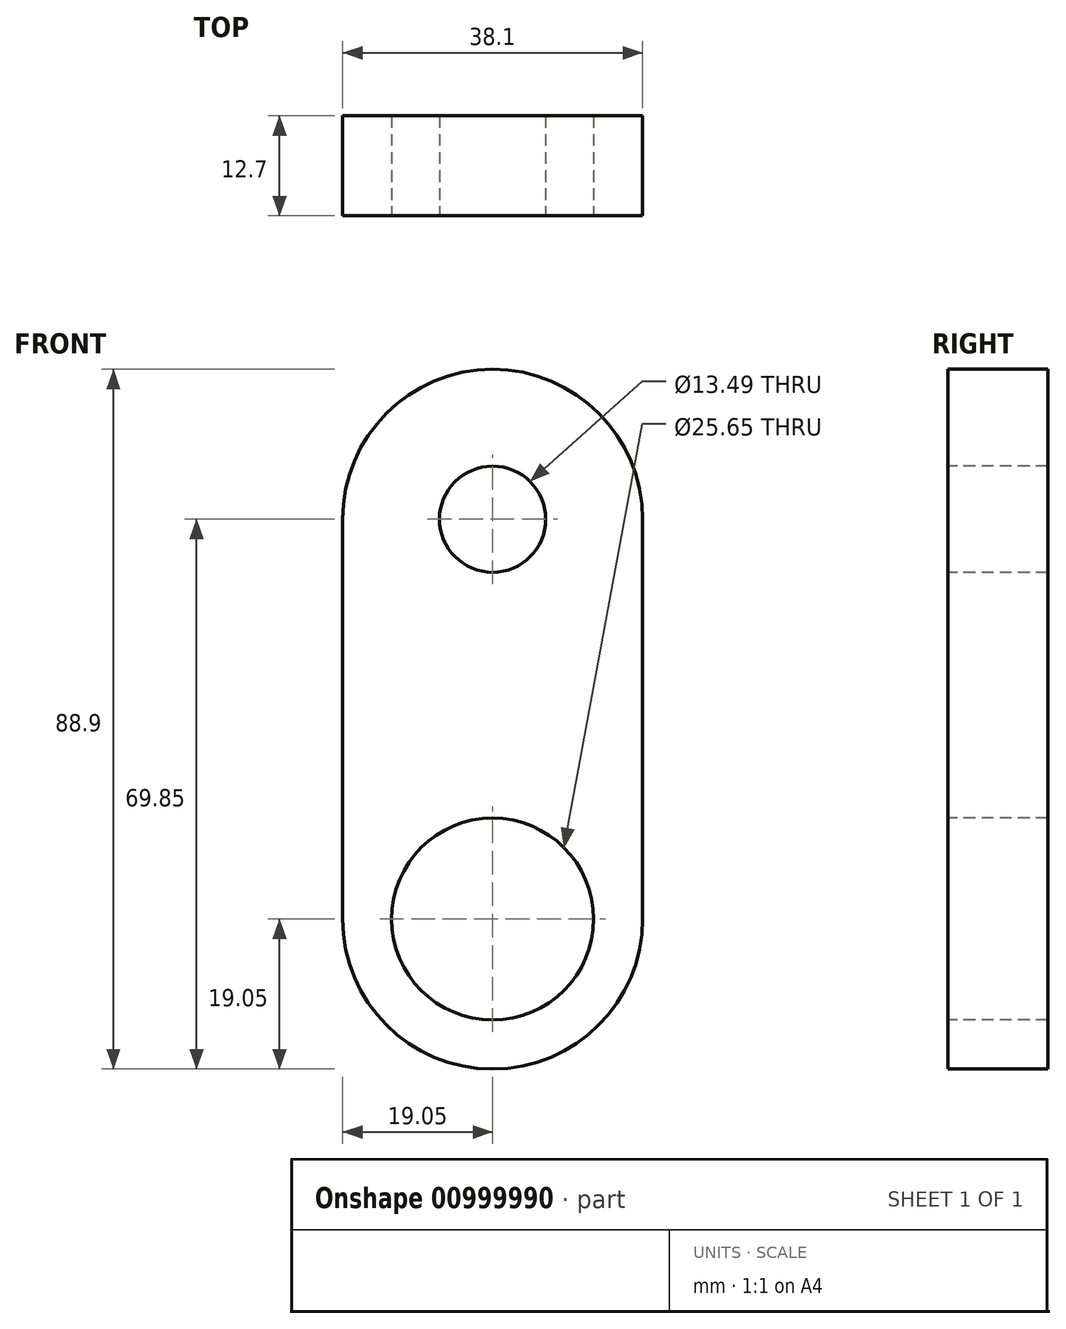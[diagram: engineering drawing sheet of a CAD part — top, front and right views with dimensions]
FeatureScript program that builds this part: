
annotation { "Feature Type Name" : "Feature", "Feature Type Description" : "" }
export const myFeature = defineFeature(function(context is Context, id is Id, definition is map)
    precondition{}
    {
        {
            var Q0;
            Q0=qCreatedBy(makeId("Front.planeOp"),FACE);
            var sketch = newSketch(context, id + "F0", { "sketchPlane" : qUnion([Q0])});
            skCircle(sketch, "E0", {"center": v(0, 0) * mm, "radius": 19.05 * mm});
            skLineSegment(sketch, "E1.bottom", {"start": v(-19.05, 0) * mm, "end": v(19.05, 0) * mm});
            skLineSegment(sketch, "E1.top", {"start": v(-19.05, 50.8) * mm, "end": v(19.05, 50.8) * mm});
            skLineSegment(sketch, "E1.left", {"start": v(-19.05, 0) * mm, "end": v(-19.05, 50.8) * mm});
            skLineSegment(sketch, "E1.right", {"start": v(19.05, 0) * mm, "end": v(19.05, 50.8) * mm});
            skCircle(sketch, "E2", {"center": v(0, 50.8) * mm, "radius": 19.05 * mm});
            skSolve(sketch);
        }
        {
            var Q0;
            {var subQ0=sQuery(id+"F0.wireOp",EDGE,"E1.top");Q0=makeQuery(id+"F0.imprint","IMPRINT",FACE,{"disambiguationData":[TD([[makeQuery(id+"F0.imprint","IMPRINT",EDGE,{"derivedFrom":subQ0}),1.0]])]});}
            var Q1;
            {var subQ0=sQuery(id+"F0.wireOp",EDGE,"E1.top");Q1=makeQuery(id+"F0.imprint","IMPRINT",FACE,{"disambiguationData":[TD([[makeQuery(id+"F0.imprint","IMPRINT",EDGE,{"derivedFrom":subQ0}),-1.0]])]});}
            var Q2;
            {var subQ0=sQuery(id+"F0.wireOp",EDGE,"E1.left");Q2=makeQuery(id+"F0.imprint","IMPRINT",FACE,{"disambiguationData":[TD([[makeQuery(id+"F0.imprint","IMPRINT",EDGE,{"derivedFrom":subQ0}),-1.0]])]});}
            var Q3;
            {var subQ0=sQuery(id+"F0.wireOp",EDGE,"E1.bottom");Q3=makeQuery(id+"F0.imprint","IMPRINT",FACE,{"disambiguationData":[TD([[makeQuery(id+"F0.imprint","IMPRINT",EDGE,{"derivedFrom":subQ0}),1.0]])]});}
            var Q4;
            {var subQ0=sQuery(id+"F0.wireOp",EDGE,"E1.bottom");Q4=makeQuery(id+"F0.imprint","IMPRINT",FACE,{"disambiguationData":[TD([[makeQuery(id+"F0.imprint","IMPRINT",EDGE,{"derivedFrom":subQ0}),-1.0]])]});}
            extrude(context, id + "F1", {"entities" : qUnion([Q0, Q1, Q2, Q3, Q4]), "depth" : 12.7 * mm, "offsetDistance" : 25.4 * mm});
        }
        {
            var Q0;
            Q0=makeQuery(id+"F1.opExtrude","CAP_FACE",FACE,{"disambiguationData":[OSD([sQuery(id+"F0.wireOp",EDGE,"E0"),sQuery(id+"F0.wireOp",EDGE,"E1.left"),sQuery(id+"F0.wireOp",EDGE,"E1.right"),sQuery(id+"F0.wireOp",EDGE,"E2")])],"isStart":false});
            var sketch = newSketch(context, id + "F2", { "sketchPlane" : qUnion([Q0])});
            skPoint(sketch, "E3", {"position": v(0, 50.8) * mm});
            skSolve(sketch);
        }
        {
            var Q0;
            Q0=makeQuery(id+"F2.imprint","IMPRINT",FACE,{"disambiguationData":[TD([[makeQuery(id+"F2.imprint","IMPRINT",EDGE,{"derivedFrom":makeQuery(id+"F1.opExtrude","CAP_EDGE",EDGE,{"disambiguationData":[OSD([sQuery(id+"F0.wireOp",EDGE,"E0")])],"isStart":false})}),1.0]])]});
            var sketch = newSketch(context, id + "F3", { "sketchPlane" : qUnion([Q0])});
            skPoint(sketch, "E4", {"position": v(0, 0) * mm});
            skSolve(sketch);
        }
        {
            var Q0;
            Q0=sQuery(id+"F2.wireOp",VERTEX,"E3");
            var Q1;
            Q1=makeQuery(id+"F1.opExtrude","SWEPT_BODY",BODY,{"disambiguationData":[OSD([sQuery(id+"F0.wireOp",EDGE,"E0"),sQuery(id+"F0.wireOp",EDGE,"E1.left"),sQuery(id+"F0.wireOp",EDGE,"E1.right"),sQuery(id+"F0.wireOp",EDGE,"E2")])]});
            hole(context, id + "F4", {"style" : HoleStyle.SIMPLE, "endStyle" : HoleEndStyle.THROUGH, "standardTappedOrClearance" : lookupTablePath({ "fit" : "Close (ASME)", "standard" : "ANSI", "size" : "1/2", "type" : "Clearance" }), "standardBlindInLast" : lookupTablePath({ "fit" : "Close", "standard" : "ANSI", "engagement" : "75%", "pitch" : "13 tpi", "size" : "1/2", "type" : "Clearance & tapped" }), "holeDiameter" : 13.5 * mm, "majorDiameter" : 6.35 * mm, "isTappedThrough" : true, "tappedDepth" : 12.7 * mm, "tapClearance" : 3, "locations" : qUnion([Q0]), "scope" : qUnion([Q1])});
        }
        {
            var Q0;
            Q0=sQuery(id+"F3.wireOp",VERTEX,"E4");
            var Q1;
            Q1=makeQuery(id+"F1.opExtrude","SWEPT_BODY",BODY,{"disambiguationData":[OSD([sQuery(id+"F0.wireOp",EDGE,"E0"),sQuery(id+"F0.wireOp",EDGE,"E1.left"),sQuery(id+"F0.wireOp",EDGE,"E1.right"),sQuery(id+"F0.wireOp",EDGE,"E2")])]});
            hole(context, id + "F5", {"style" : HoleStyle.SIMPLE, "endStyle" : HoleEndStyle.THROUGH, "holeDiameter" : 25.65 * mm, "majorDiameter" : 6.35 * mm, "isTappedThrough" : true, "tappedDepth" : 12.7 * mm, "tapClearance" : 3, "locations" : qUnion([Q0]), "scope" : qUnion([Q1])});
        }
    });
